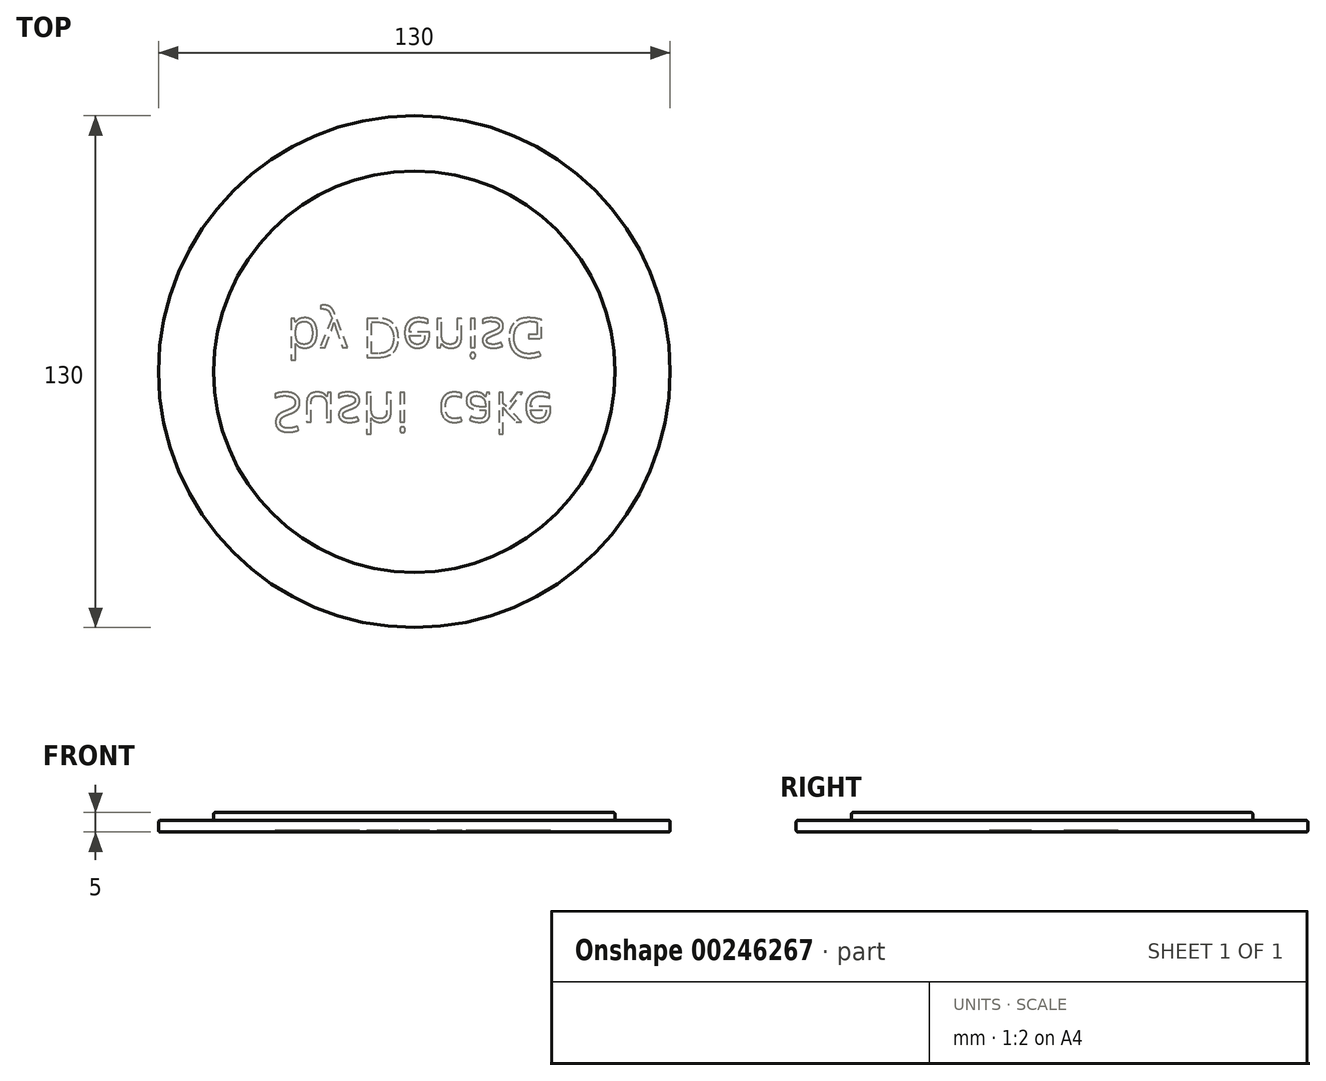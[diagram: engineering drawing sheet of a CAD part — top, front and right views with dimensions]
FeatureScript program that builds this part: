
annotation { "Feature Type Name" : "Feature", "Feature Type Description" : "" }
export const myFeature = defineFeature(function(context is Context, id is Id, definition is map)
    precondition{}
    {
        {
            var Q0;
            Q0=qCreatedBy(makeId("Top.planeOp"),FACE);
            var sketch = newSketch(context, id + "F0", { "sketchPlane" : qUnion([Q0])});
            skCircle(sketch, "E0", {"center": v(0, 0) * mm, "radius": 65 * mm});
            skSolve(sketch);
        }
        {
            var Q0;
            Q0 = qSketchRegion(id + "F0", true);
            extrude(context, id + "F1", {"entities" : qUnion([Q0]), "depth" : 3 * mm});
        }
        {
            var Q0;
            Q0=makeQuery(id+"F1.opExtrude","CAP_FACE",FACE,{"disambiguationData":[OSD([sQuery(id+"F0.wireOp",EDGE,"E0")])],"isStart":false});
            var sketch = newSketch(context, id + "F2", { "sketchPlane" : qUnion([Q0])});
            skCircle(sketch, "E1", {"center": v(0, 0) * mm, "radius": 51 * mm});
            skSolve(sketch);
        }
        {
            var Q0;
            Q0 = qSketchRegion(id + "F2", true);
            extrude(context, id + "F3", {"entities" : qUnion([Q0]), "operationType" : NewBodyOperationType.ADD, "depth" : 2 * mm});
        }
        {
            var Q0;
            Q0=makeQuery(id+"F1.opExtrude","SWEPT_FACE",FACE,{"disambiguationData":[OSD([sQuery(id+"F0.wireOp",EDGE,"E0")])]});
            var Q1;
            Q1=makeQuery(id+"F3.opExtrude","CAP_EDGE",EDGE,{"disambiguationData":[OSD([sQuery(id+"F2.wireOp",EDGE,"E1")])],"isStart":false});
            fillet(context, id + "F4", {"entities" : qUnion([Q0, Q1]), "radius" : 0.5 * mm, "tangentPropagation" : true, "allowEdgeOverflow" : false});
        }
        {
            var Q0;
            Q0=makeQuery(id+"F1.opExtrude","CAP_FACE",FACE,{"disambiguationData":[OSD([sQuery(id+"F0.wireOp",EDGE,"E0")])],"isStart":true});
            var sketch = newSketch(context, id + "F5", { "sketchPlane" : qUnion([Q0])});
            skText(sketch, "E2", { "text": "Sushi  cake\n by DenisG", "fontName": "OpenSans-Regular.ttf"});
            const initialGuessF5  = {"E2": [-0.03608, 0.00534, 1, 0, 0.01]};
            skSetInitialGuess(sketch, initialGuessF5);
            skSolve(sketch);
        }
        {
            var Q0;
            Q0 = qSketchRegion(id + "F5", true);
            extrude(context, id + "F6", {"entities" : qUnion([Q0]), "operationType" : NewBodyOperationType.REMOVE, "oppositeDirection" : true, "depth" : 0.5 * mm});
        }
    });
